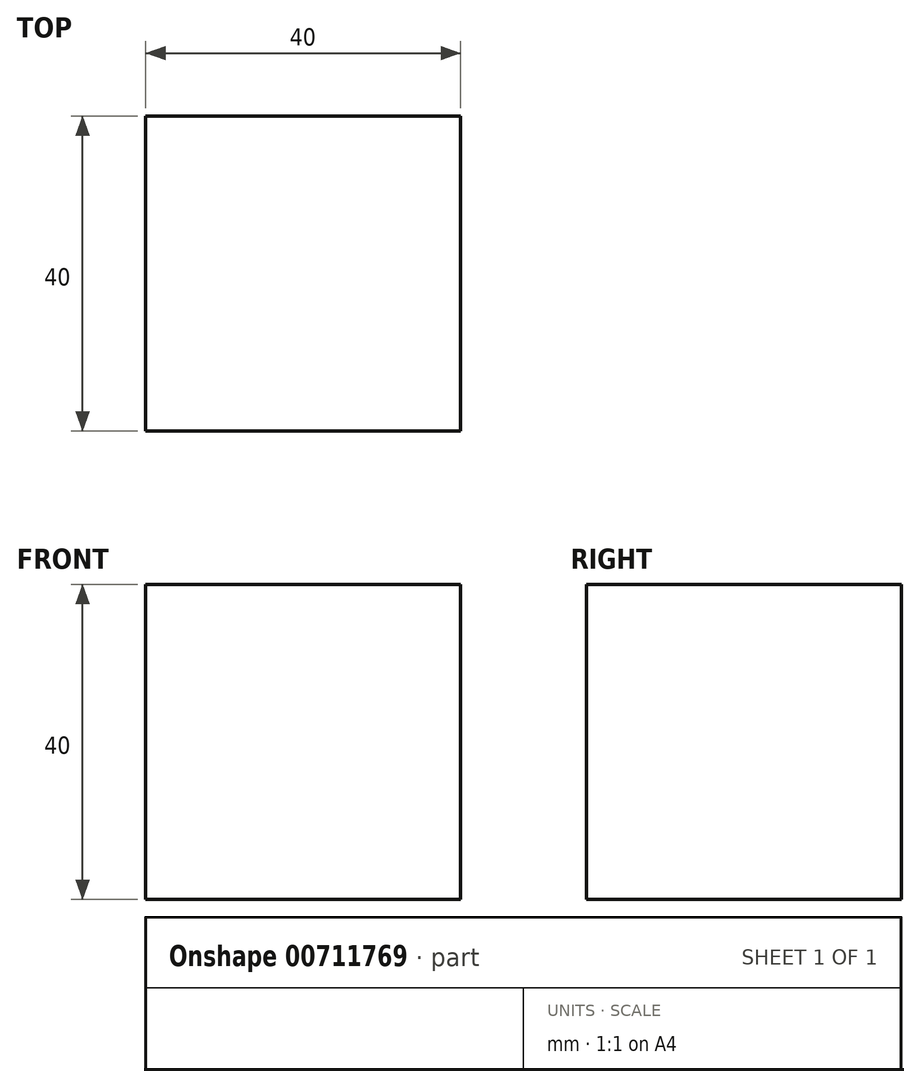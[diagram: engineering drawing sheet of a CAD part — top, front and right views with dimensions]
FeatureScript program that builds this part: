
annotation { "Feature Type Name" : "Feature", "Feature Type Description" : "" }
export const myFeature = defineFeature(function(context is Context, id is Id, definition is map)
    precondition{}
    {
        {
            var Q0;
            Q0=qCreatedBy(makeId("Front.planeOp"),FACE);
            var sketch = newSketch(context, id + "F0", { "sketchPlane" : qUnion([Q0])});
            skLineSegment(sketch, "E0.bottom", {"start": v(20, 20) * mm, "end": v(-20, 20) * mm});
            skLineSegment(sketch, "E0.top", {"start": v(20, -20) * mm, "end": v(-20, -20) * mm});
            skLineSegment(sketch, "E0.left", {"start": v(20, 20) * mm, "end": v(20, -20) * mm});
            skLineSegment(sketch, "E0.right", {"start": v(-20, 20) * mm, "end": v(-20, -20) * mm});
            skPoint(sketch, "E0.middle", {"position": v(0, 0) * mm});
            skSolve(sketch);
        }
        {
            var Q0;
            Q0=makeQuery(id+"F0.imprint","IMPRINT",FACE,{"disambiguationData":[TD([[makeQuery(id+"F0.imprint","IMPRINT",EDGE,{"derivedFrom":sQuery(id+"F0.wireOp",EDGE,"E0.bottom")}),1.0]])]});
            extrude(context, id + "F1", {"entities" : qUnion([Q0]), "endBound" : BoundingType.SYMMETRIC, "depth" : 40 * mm, "offsetDistance" : 25.4 * mm});
        }
    });
